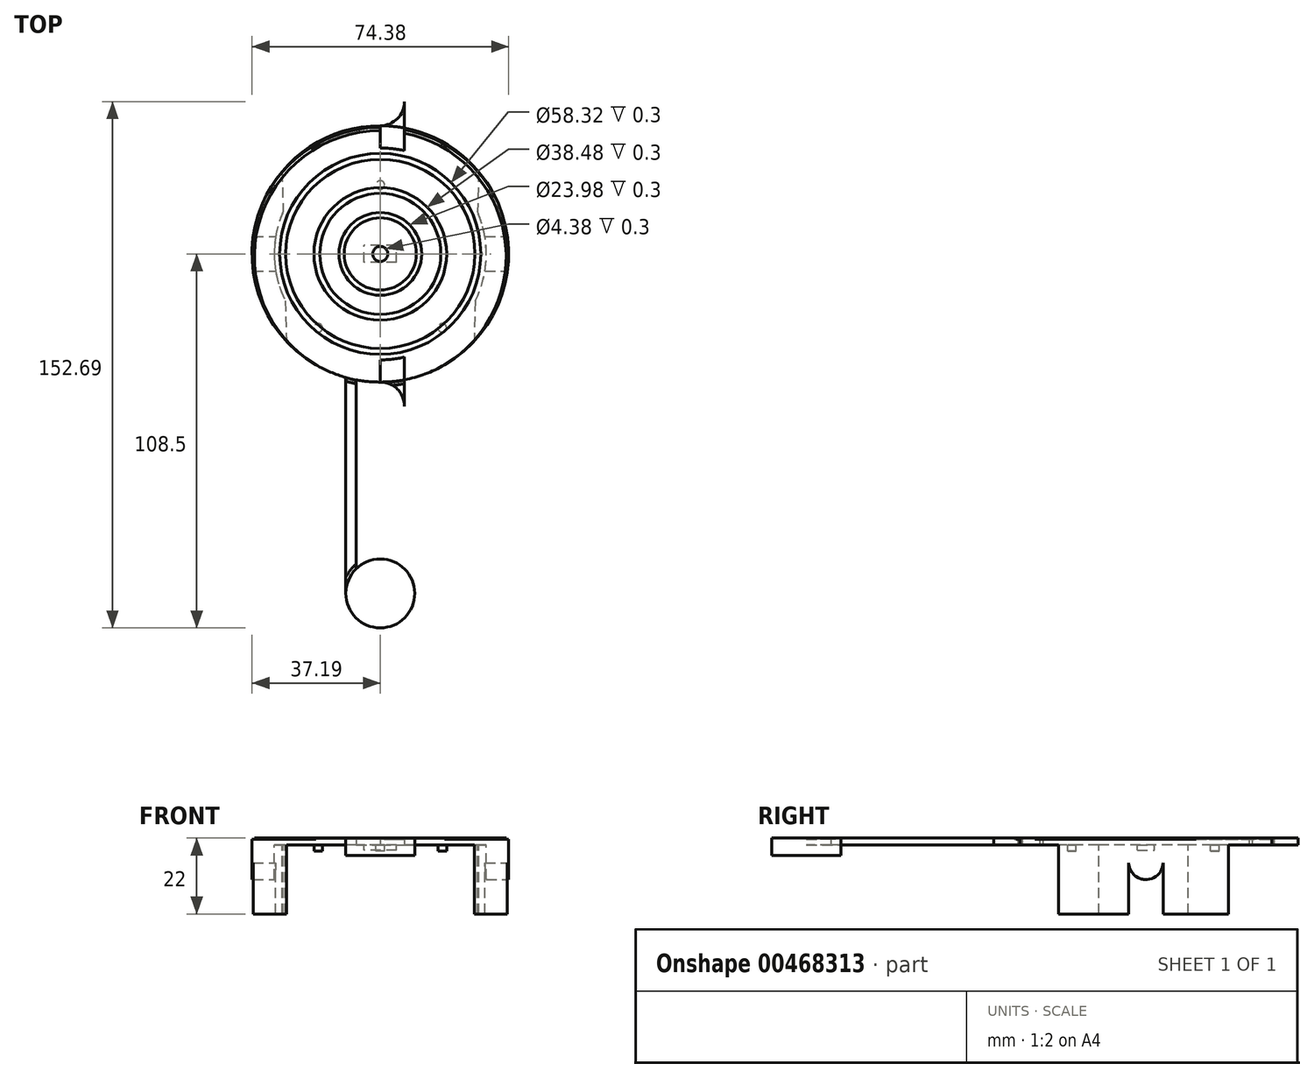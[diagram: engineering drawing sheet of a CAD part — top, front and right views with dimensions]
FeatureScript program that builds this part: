
annotation { "Feature Type Name" : "Feature", "Feature Type Description" : "" }
export const myFeature = defineFeature(function(context is Context, id is Id, definition is map)
    precondition{}
    {
        {
            var Q0;
            Q0=qCreatedBy(makeId("Top.planeOp"),FACE);
            var sketch = newSketch(context, id + "F0", { "sketchPlane" : qUnion([Q0])});
            skLineSegment(sketch, "E0.bottom", {"start": v(4.75, -2.5) * mm, "end": v(-4.75, -2.5) * mm});
            skLineSegment(sketch, "E0.top", {"start": v(4.75, 2.5) * mm, "end": v(-4.75, 2.5) * mm});
            skLineSegment(sketch, "E0.left", {"start": v(4.75, -2.5) * mm, "end": v(4.75, 2.5) * mm});
            skLineSegment(sketch, "E0.right", {"start": v(-4.75, -2.5) * mm, "end": v(-4.75, 2.5) * mm});
            skPoint(sketch, "E0.middle", {"position": v(0, 0) * mm});
            skLineSegment(sketch, "E1.bottom", {"start": v(5.25, 3) * mm, "end": v(-5.25, 3) * mm});
            skLineSegment(sketch, "E1.top", {"start": v(5.25, -3) * mm, "end": v(-5.25, -3) * mm});
            skLineSegment(sketch, "E1.left", {"start": v(5.25, 3) * mm, "end": v(5.25, -3) * mm});
            skLineSegment(sketch, "E1.right", {"start": v(-5.25, 3) * mm, "end": v(-5.25, -3) * mm});
            skCircle(sketch, "E2", {"center": v(0, 0) * mm, "radius": 37.2 * mm});
            skLineSegment(sketch, "E3", {"start": v(0, 0) * mm, "end": v(18, -21.45) * mm, "construction": true});
            skLineSegment(sketch, "E4", {"start": v(18, -21.45) * mm, "end": v(-18, -21.45) * mm});
            skLineSegment(sketch, "E5", {"start": v(-18, -21.45) * mm, "end": v(0, 0) * mm, "construction": true});
            skLineSegment(sketch, "E6", {"start": v(0, 0) * mm, "end": v(0, 20) * mm, "construction": true});
            skPoint(sketch, "E6.endSnap0", {"position": v(0, 3) * mm});
            skCircle(sketch, "E7", {"center": v(0, 20) * mm, "radius": 1.25 * mm});
            skCircle(sketch, "E8", {"center": v(18, -21.45) * mm, "radius": 1.25 * mm});
            skCircle(sketch, "E9", {"center": v(-18, -21.45) * mm, "radius": 1.25 * mm});
            skLineSegment(sketch, "E10", {"start": v(28.5, 23.9) * mm, "end": v(-28.5, 23.9) * mm, "construction": true});
            skLineSegment(sketch, "E11", {"start": v(27.25, -25.31) * mm, "end": v(-27.25, -25.31) * mm, "construction": true});
            skLineSegment(sketch, "E12", {"start": v(28.5, 23.9) * mm, "end": v(27.25, -25.31) * mm});
            skLineSegment(sketch, "E13", {"start": v(-28.5, 23.9) * mm, "end": v(-27.25, -25.31) * mm});
            skLineSegment(sketch, "E14", {"start": v(0, 0) * mm, "end": v(0, 108) * mm, "construction": true});
            skLineSegment(sketch, "E15", {"start": v(0, 0) * mm, "end": v(0, -98.5) * mm, "construction": true});
            skLineSegment(sketch, "E16.bottom", {"start": v(0, 108) * mm, "end": v(0, 108) * mm});
            skLineSegment(sketch, "E16.top", {"start": v(0, -98.5) * mm, "end": v(0, -98.5) * mm});
            skLineSegment(sketch, "E16.left", {"start": v(0, 108) * mm, "end": v(0, -98.5) * mm});
            skLineSegment(sketch, "E16.right", {"start": v(0, 108) * mm, "end": v(0, -98.5) * mm});
            skLineSegment(sketch, "E17.bottom", {"start": v(10, -98.5) * mm, "end": v(-10, -98.5) * mm});
            skLineSegment(sketch, "E17.top", {"start": v(10, 108) * mm, "end": v(-10, 108) * mm});
            skLineSegment(sketch, "E17.left", {"start": v(10, -98.5) * mm, "end": v(10, 108) * mm});
            skLineSegment(sketch, "E17.right", {"start": v(-10, -98.5) * mm, "end": v(-10, 108) * mm});
            skPoint(sketch, "E17.middle", {"position": v(0, 4.75) * mm});
            skCircle(sketch, "E18", {"center": v(0, 108) * mm, "radius": 10 * mm});
            skCircle(sketch, "E19", {"center": v(0, -98.5) * mm, "radius": 10 * mm});
            skCircle(sketch, "E20.0", {"center": v(0, 108) * mm, "radius": 7 * mm});
            skCircle(sketch, "E21", {"center": v(0, -98.5) * mm, "radius": 7 * mm});
            skLineSegment(sketch, "E22", {"start": v(7, 108) * mm, "end": v(7, -98.5) * mm});
            skLineSegment(sketch, "E23", {"start": v(-7, 108) * mm, "end": v(-7, -98.5) * mm});
            skLineSegment(sketch, "E24", {"start": v(-10, 37.2) * mm, "end": v(7, 37.2) * mm, "construction": true});
            skPoint(sketch, "E25", {"position": v(0, 37.2) * mm});
            skCircle(sketch, "E26", {"center": v(0, 44.2) * mm, "radius": 7 * mm});
            skPoint(sketch, "E27", {"position": v(0, -37.2) * mm});
            skCircle(sketch, "E28", {"center": v(0, -44.2) * mm, "radius": 7 * mm});
            skCircle(sketch, "E29", {"center": v(0, 108) * mm, "radius": 6.5 * mm});
            skCircle(sketch, "E30", {"center": v(0, 0) * mm, "radius": 30.75 * mm});
            skSolve(sketch);
        }
        {
            var Q0;
            {var subQ0=sQuery(id+"F0.wireOp",EDGE,"E12");Q0=makeQuery(id+"F0.imprint","IMPRINT",FACE,{"disambiguationData":[TD([[makeQuery(id+"F0.imprint","IMPRINT",EDGE,{"derivedFrom":subQ0}),1.0]])]});}
            var Q1;
            {var subQ0=sQuery(id+"F0.wireOp",EDGE,"E13");Q1=makeQuery(id+"F0.imprint","IMPRINT",FACE,{"disambiguationData":[TD([[makeQuery(id+"F0.imprint","IMPRINT",EDGE,{"derivedFrom":subQ0}),-1.0]])]});}
            extrude(context, id + "F1", {"entities" : qUnion([Q0, Q1]), "depth" : -20 * mm});
        }
        {
            var Q0;
            Q0=qCreatedBy(makeId("Right.planeOp"),FACE);
            var sketch = newSketch(context, id + "F2", { "sketchPlane" : qUnion([Q0])});
            skLineSegment(sketch, "E31.0.0", {"start": v(-13.66, 0) * mm, "end": v(12.25, 0) * mm});
            skLineSegment(sketch, "E31.0.1", {"start": v(12.25, 0) * mm, "end": v(12.25, -20) * mm});
            skLineSegment(sketch, "E31.0.2", {"start": v(12.25, -20) * mm, "end": v(-13.66, -20) * mm});
            skLineSegment(sketch, "E31.0.3", {"start": v(-13.66, -20) * mm, "end": v(-13.66, 0) * mm});
            skLineSegment(sketch, "E32.bottom", {"start": v(-5, 0) * mm, "end": v(5, 0) * mm});
            skLineSegment(sketch, "E32.top", {"start": v(-5, -20) * mm, "end": v(5, -20) * mm});
            skLineSegment(sketch, "E32.left", {"start": v(-5, 0) * mm, "end": v(-5, -20) * mm});
            skLineSegment(sketch, "E32.right", {"start": v(5, 0) * mm, "end": v(5, -20) * mm});
            skPoint(sketch, "E32.middle", {"position": v(0, -10) * mm});
            skCircle(sketch, "E33", {"center": v(0, -5) * mm, "radius": 5 * mm});
            skPoint(sketch, "E33.first.point", {"position": v(5, -5.19) * mm});
            skPoint(sketch, "E33.second.point", {"position": v(0, 0) * mm});
            skPoint(sketch, "E33.third.point", {"position": v(-5, -4.77) * mm});
            skSolve(sketch);
        }
        {
            var Q0;
            {var subQ0=sQuery(id+"F2.wireOp",EDGE,"E32.top");Q0=makeQuery(id+"F2.imprint","IMPRINT",FACE,{"disambiguationData":[TD([[makeQuery(id+"F2.imprint","IMPRINT",EDGE,{"derivedFrom":subQ0}),1.0]])]});}
            var Q1;
            {var subQ0=sQuery(id+"F2.wireOp",EDGE,"E33");var subQ2=sQuery(id+"F2.wireOp",EDGE,"E32.left");var subQ3=makeQuery(id+"F2.imprint","INTERSECT",VERTEX,{"disambiguationData":[OD(0.0)],"derivedFrom":[subQ2,subQ0]});Q1=makeQuery(id+"F2.imprint","IMPRINT",FACE,{"disambiguationData":[TD([[makeQuery(id+"F2.imprint","IMPRINT",EDGE,{"disambiguationData":[TD([[subQ3,-1.0]])],"derivedFrom":subQ2}),1.0]])]});}
            extrude(context, id + "F3", {"entities" : qUnion([Q0, Q1]), "operationType" : NewBodyOperationType.REMOVE, "endBound" : BoundingType.THROUGH_ALL, "oppositeDirection" : true, "depth" : 25 * mm, "hasSecondDirection" : true, "secondDirectionBound" : SecondDirectionBoundingType.THROUGH_ALL, "secondDirectionOppositeDirection" : false, "secondDirectionDepth" : 25 * mm});
        }
        {
            var Q0;
            Q0=makeQuery(id+"F0.imprint","IMPRINT",FACE,{"disambiguationData":[TD([[makeQuery(id+"F0.imprint","IMPRINT",EDGE,{"derivedFrom":sQuery(id+"F0.wireOp",EDGE,"E9")}),1.0]])]});
            var Q1;
            Q1=makeQuery(id+"F0.imprint","IMPRINT",FACE,{"disambiguationData":[TD([[makeQuery(id+"F0.imprint","IMPRINT",EDGE,{"derivedFrom":sQuery(id+"F0.wireOp",EDGE,"E8")}),1.0]])]});
            var Q2;
            Q2=makeQuery(id+"F0.imprint","IMPRINT",FACE,{"disambiguationData":[TD([[makeQuery(id+"F0.imprint","IMPRINT",EDGE,{"derivedFrom":sQuery(id+"F0.wireOp",EDGE,"E7")}),1.0]])]});
            extrude(context, id + "F4", {"entities" : qUnion([Q0, Q1, Q2]), "operationType" : NewBodyOperationType.ADD, "depth" : -1.75 * mm});
        }
        {
            var Q0;
            Q0=makeQuery(id+"F0.imprint","IMPRINT",FACE,{"disambiguationData":[TD([[makeQuery(id+"F0.imprint","IMPRINT",EDGE,{"derivedFrom":sQuery(id+"F0.wireOp",EDGE,"E0.bottom")}),-1.0]])]});
            var Q1;
            Q1=makeQuery(id+"F0.imprint","IMPRINT",FACE,{"disambiguationData":[TD([[makeQuery(id+"F0.imprint","IMPRINT",EDGE,{"derivedFrom":sQuery(id+"F0.wireOp",EDGE,"E1.bottom")}),-1.0]])]});
            var Q2;
            Q2=makeQuery(id+"F0.imprint","IMPRINT",FACE,{"disambiguationData":[TD([[makeQuery(id+"F0.imprint","IMPRINT",EDGE,{"derivedFrom":sQuery(id+"F0.wireOp",EDGE,"E0.bottom")}),1.0]])]});
            var Q3;
            Q3=makeQuery(id+"F4.opExtrude","CAP_FACE",FACE,{"disambiguationData":[OSD([sQuery(id+"F0.wireOp",EDGE,"E7")])],"isStart":true});
            var Q4;
            Q4=makeQuery(id+"F4.opExtrude","CAP_FACE",FACE,{"disambiguationData":[OSD([sQuery(id+"F0.wireOp",EDGE,"E9")])],"isStart":true});
            var Q5;
            Q5=makeQuery(id+"F4.opExtrude","CAP_FACE",FACE,{"disambiguationData":[OSD([sQuery(id+"F0.wireOp",EDGE,"E8")])],"isStart":true});
            var Q6;
            Q6=makeQuery(id+"F0.imprint","IMPRINT",FACE,{"disambiguationData":[TD([[makeQuery(id+"F0.imprint","IMPRINT",EDGE,{"derivedFrom":sQuery(id+"F0.wireOp",EDGE,"E7")}),1.0]])]});
            var Q7;
            Q7=makeQuery(id+"F0.imprint","IMPRINT",FACE,{"disambiguationData":[TD([[makeQuery(id+"F0.imprint","IMPRINT",EDGE,{"derivedFrom":sQuery(id+"F0.wireOp",EDGE,"E8")}),1.0]])]});
            var Q8;
            Q8=makeQuery(id+"F4.opExtrude","CAP_FACE",FACE,{"disambiguationData":[OSD([sQuery(id+"F0.wireOp",EDGE,"E7")])],"isStart":false});
            var Q9;
            Q9=makeQuery(id+"F4.opExtrude","CAP_FACE",FACE,{"disambiguationData":[OSD([sQuery(id+"F0.wireOp",EDGE,"E9")])],"isStart":false});
            var Q10;
            Q10=makeQuery(id+"F4.opExtrude","CAP_FACE",FACE,{"disambiguationData":[OSD([sQuery(id+"F0.wireOp",EDGE,"E8")])],"isStart":false});
            var Q11;
            {var subQ0=sQuery(id+"F0.wireOp",EDGE,"E12");Q11=makeQuery(id+"F0.imprint","IMPRINT",FACE,{"disambiguationData":[TD([[makeQuery(id+"F0.imprint","IMPRINT",EDGE,{"derivedFrom":subQ0}),1.0]])]});}
            var Q12;
            {var subQ0=sQuery(id+"F0.wireOp",EDGE,"E13");Q12=makeQuery(id+"F0.imprint","IMPRINT",FACE,{"disambiguationData":[TD([[makeQuery(id+"F0.imprint","IMPRINT",EDGE,{"derivedFrom":subQ0}),-1.0]])]});}
            var Q13;
            Q13=makeQuery(id+"F0.imprint","IMPRINT",FACE,{"disambiguationData":[TD([[makeQuery(id+"F0.imprint","IMPRINT",EDGE,{"derivedFrom":sQuery(id+"F0.wireOp",EDGE,"E9")}),-1.0]])]});
            var Q14;
            Q14=makeQuery(id+"F0.imprint","IMPRINT",FACE,{"disambiguationData":[TD([[makeQuery(id+"F0.imprint","IMPRINT",EDGE,{"derivedFrom":sQuery(id+"F0.wireOp",EDGE,"E8")}),-1.0]])]});
            var Q15;
            {var subQ0=sQuery(id+"F0.wireOp",EDGE,"E17.left");var subQ1=sQuery(id+"F0.wireOp",EDGE,"E2");var subQ2=makeQuery(id+"F0.imprint","INTERSECT",VERTEX,{"disambiguationData":[OD(1.0)],"derivedFrom":[subQ1,subQ0]});Q15=makeQuery(id+"F0.imprint","IMPRINT",FACE,{"disambiguationData":[TD([[makeQuery(id+"F0.imprint","IMPRINT",EDGE,{"disambiguationData":[TD([[subQ2,1.0]])],"derivedFrom":subQ1}),1.0]])]});}
            var Q16;
            {var subQ0=sQuery(id+"F0.wireOp",EDGE,"E17.right");var subQ1=sQuery(id+"F0.wireOp",EDGE,"E2");var subQ2=makeQuery(id+"F0.imprint","INTERSECT",VERTEX,{"disambiguationData":[OD(1.0)],"derivedFrom":[subQ1,subQ0]});Q16=makeQuery(id+"F0.imprint","IMPRINT",FACE,{"disambiguationData":[TD([[makeQuery(id+"F0.imprint","IMPRINT",EDGE,{"disambiguationData":[TD([[subQ2,-1.0]])],"derivedFrom":subQ1}),1.0]])]});}
            var Q17;
            {var subQ0=sQuery(id+"F0.wireOp",EDGE,"E23");var subQ1=sQuery(id+"F0.wireOp",EDGE,"E2");var subQ2=makeQuery(id+"F0.imprint","INTERSECT",VERTEX,{"disambiguationData":[OD(1.0)],"derivedFrom":[subQ1,subQ0]});Q17=makeQuery(id+"F0.imprint","IMPRINT",FACE,{"disambiguationData":[TD([[makeQuery(id+"F0.imprint","IMPRINT",EDGE,{"disambiguationData":[TD([[subQ2,-1.0]])],"derivedFrom":subQ1}),1.0]])]});}
            var Q18;
            {var subQ1=sQuery(id+"F0.wireOp",EDGE,"E2");var subQ7=sQuery(id+"F0.wireOp",EDGE,"JaR2KPRH-AKVw-h21Q-BMjd-ttM7igPpjMCP");var subQ9=makeQuery(id+"F0.imprint","INTERSECT",VERTEX,{"disambiguationData":[OD(1.0)],"derivedFrom":[subQ1,subQ7]});Q18=makeQuery(id+"F0.imprint","IMPRINT",FACE,{"disambiguationData":[TD([[makeQuery(id+"F0.imprint","IMPRINT",EDGE,{"disambiguationData":[TD([[subQ9,-1.0]])],"derivedFrom":subQ1}),1.0]])]});}
            var Q19;
            {var subQ0=sQuery(id+"F0.wireOp",EDGE,"E17.right");var subQ1=sQuery(id+"F0.wireOp",EDGE,"E2");var subQ2=makeQuery(id+"F0.imprint","INTERSECT",VERTEX,{"disambiguationData":[OD(0.0)],"derivedFrom":[subQ1,subQ0]});Q19=makeQuery(id+"F0.imprint","IMPRINT",FACE,{"disambiguationData":[TD([[makeQuery(id+"F0.imprint","IMPRINT",EDGE,{"disambiguationData":[TD([[subQ2,1.0]])],"derivedFrom":subQ1}),1.0]])]});}
            var Q20;
            {var subQ0=sQuery(id+"F0.wireOp",EDGE,"E17.left");var subQ1=sQuery(id+"F0.wireOp",EDGE,"E2");var subQ2=makeQuery(id+"F0.imprint","INTERSECT",VERTEX,{"disambiguationData":[OD(0.0)],"derivedFrom":[subQ1,subQ0]});Q20=makeQuery(id+"F0.imprint","IMPRINT",FACE,{"disambiguationData":[TD([[makeQuery(id+"F0.imprint","IMPRINT",EDGE,{"disambiguationData":[TD([[subQ2,-1.0]])],"derivedFrom":subQ1}),1.0]])]});}
            var Q21;
            {var subQ0=sQuery(id+"F0.wireOp",EDGE,"E22");var subQ5=sQuery(id+"F0.wireOp",EDGE,"E4");var subQ6=makeQuery(id+"F0.imprint","INTERSECT",VERTEX,{"derivedFrom":[subQ5,subQ0]});Q21=makeQuery(id+"F0.imprint","IMPRINT",FACE,{"disambiguationData":[TD([[makeQuery(id+"F0.imprint","IMPRINT",EDGE,{"disambiguationData":[TD([[subQ6,-1.0]])],"derivedFrom":subQ5}),1.0]])]});}
            var Q22;
            {var subQ11=sQuery(id+"F0.wireOp",EDGE,"E1.left");Q22=makeQuery(id+"F0.imprint","IMPRINT",FACE,{"disambiguationData":[TD([[makeQuery(id+"F0.imprint","IMPRINT",EDGE,{"derivedFrom":subQ11}),1.0]])]});}
            var Q23;
            {var subQ0=sQuery(id+"F0.wireOp",EDGE,"E13");var subQ1=sQuery(id+"F0.wireOp",EDGE,"E2");var subQ2=makeQuery(id+"F0.imprint","INTERSECT",VERTEX,{"disambiguationData":[OD(0.0)],"derivedFrom":[subQ1,subQ0]});Q23=makeQuery(id+"F0.imprint","IMPRINT",FACE,{"disambiguationData":[TD([[makeQuery(id+"F0.imprint","IMPRINT",EDGE,{"disambiguationData":[TD([[subQ2,1.0]])],"derivedFrom":subQ1}),1.0]])]});}
            var Q24;
            {var subQ0=sQuery(id+"F0.wireOp",EDGE,"E23");var subQ1=sQuery(id+"F0.wireOp",EDGE,"E2");var subQ2=makeQuery(id+"F0.imprint","INTERSECT",VERTEX,{"disambiguationData":[OD(0.0)],"derivedFrom":[subQ1,subQ0]});Q24=makeQuery(id+"F0.imprint","IMPRINT",FACE,{"disambiguationData":[TD([[makeQuery(id+"F0.imprint","IMPRINT",EDGE,{"disambiguationData":[TD([[subQ2,-1.0]])],"derivedFrom":subQ0}),1.0]])]});}
            var Q25;
            {var subQ0=sQuery(id+"F0.wireOp",EDGE,"E22");var subQ1=sQuery(id+"F0.wireOp",EDGE,"E2");var subQ2=makeQuery(id+"F0.imprint","INTERSECT",VERTEX,{"disambiguationData":[OD(0.0)],"derivedFrom":[subQ1,subQ0]});Q25=makeQuery(id+"F0.imprint","IMPRINT",FACE,{"disambiguationData":[TD([[makeQuery(id+"F0.imprint","IMPRINT",EDGE,{"disambiguationData":[TD([[subQ2,-1.0]])],"derivedFrom":subQ0}),-1.0]])]});}
            var Q26;
            {var subQ0=sQuery(id+"F0.wireOp",EDGE,"E12");var subQ1=sQuery(id+"F0.wireOp",EDGE,"E2");var subQ2=makeQuery(id+"F0.imprint","INTERSECT",VERTEX,{"disambiguationData":[OD(0.0)],"derivedFrom":[subQ1,subQ0]});Q26=makeQuery(id+"F0.imprint","IMPRINT",FACE,{"disambiguationData":[TD([[makeQuery(id+"F0.imprint","IMPRINT",EDGE,{"disambiguationData":[TD([[subQ2,-1.0]])],"derivedFrom":subQ1}),1.0]])]});}
            var Q27;
            {var subQ0=sQuery(id+"F0.wireOp",EDGE,"E17.left");var subQ1=sQuery(id+"F0.wireOp",EDGE,"E4");var subQ2=makeQuery(id+"F0.imprint","INTERSECT",VERTEX,{"derivedFrom":[subQ1,subQ0]});Q27=makeQuery(id+"F0.imprint","IMPRINT",FACE,{"disambiguationData":[TD([[makeQuery(id+"F0.imprint","IMPRINT",EDGE,{"disambiguationData":[TD([[subQ2,-1.0]])],"derivedFrom":subQ1}),-1.0]])]});}
            var Q28;
            {var subQ0=sQuery(id+"F0.wireOp",EDGE,"E17.right");var subQ1=sQuery(id+"F0.wireOp",EDGE,"E4");var subQ2=makeQuery(id+"F0.imprint","INTERSECT",VERTEX,{"derivedFrom":[subQ1,subQ0]});Q28=makeQuery(id+"F0.imprint","IMPRINT",FACE,{"disambiguationData":[TD([[makeQuery(id+"F0.imprint","IMPRINT",EDGE,{"disambiguationData":[TD([[subQ2,1.0]])],"derivedFrom":subQ1}),-1.0]])]});}
            var Q29;
            {var subQ0=sQuery(id+"F0.wireOp",EDGE,"E30");var subQ1=sQuery(id+"F0.wireOp",EDGE,"E12");var subQ2=makeQuery(id+"F0.imprint","INTERSECT",VERTEX,{"disambiguationData":[OD(0.0)],"derivedFrom":[subQ1,subQ0]});Q29=makeQuery(id+"F0.imprint","IMPRINT",FACE,{"disambiguationData":[TD([[makeQuery(id+"F0.imprint","IMPRINT",EDGE,{"disambiguationData":[TD([[subQ2,-1.0]])],"derivedFrom":subQ1}),1.0]])]});}
            var Q30;
            {var subQ0=sQuery(id+"F0.wireOp",EDGE,"E12");var subQ1=sQuery(id+"F0.wireOp",EDGE,"E2");var subQ2=makeQuery(id+"F0.imprint","INTERSECT",VERTEX,{"disambiguationData":[OD(1.0)],"derivedFrom":[subQ1,subQ0]});Q30=makeQuery(id+"F0.imprint","IMPRINT",FACE,{"disambiguationData":[TD([[makeQuery(id+"F0.imprint","IMPRINT",EDGE,{"disambiguationData":[TD([[subQ2,1.0]])],"derivedFrom":subQ1}),1.0]])]});}
            var Q31;
            {var subQ0=sQuery(id+"F0.wireOp",EDGE,"E22");var subQ1=sQuery(id+"F0.wireOp",EDGE,"E2");var subQ2=makeQuery(id+"F0.imprint","INTERSECT",VERTEX,{"disambiguationData":[OD(1.0)],"derivedFrom":[subQ1,subQ0]});Q31=makeQuery(id+"F0.imprint","IMPRINT",FACE,{"disambiguationData":[TD([[makeQuery(id+"F0.imprint","IMPRINT",EDGE,{"disambiguationData":[TD([[subQ2,1.0]])],"derivedFrom":subQ0}),-1.0]])]});}
            var Q32;
            {var subQ0=sQuery(id+"F0.wireOp",EDGE,"E17.left");var subQ1=sQuery(id+"F0.wireOp",EDGE,"E4");var subQ2=makeQuery(id+"F0.imprint","INTERSECT",VERTEX,{"derivedFrom":[subQ1,subQ0]});Q32=makeQuery(id+"F0.imprint","IMPRINT",FACE,{"disambiguationData":[TD([[makeQuery(id+"F0.imprint","IMPRINT",EDGE,{"disambiguationData":[TD([[subQ2,-1.0]])],"derivedFrom":subQ1}),1.0]])]});}
            var Q33;
            {var subQ0=sQuery(id+"F0.wireOp",EDGE,"E16.left");var subQ1=sQuery(id+"F0.wireOp",EDGE,"E4");var subQ2=makeQuery(id+"F0.imprint","INTERSECT",VERTEX,{"derivedFrom":[subQ1,subQ0]});Q33=makeQuery(id+"F0.imprint","IMPRINT",FACE,{"disambiguationData":[TD([[makeQuery(id+"F0.imprint","IMPRINT",EDGE,{"disambiguationData":[TD([[subQ2,-1.0]])],"derivedFrom":subQ1}),1.0]])]});}
            var Q34;
            {var subQ0=sQuery(id+"F0.wireOp",EDGE,"E17.right");var subQ1=sQuery(id+"F0.wireOp",EDGE,"E4");var subQ2=makeQuery(id+"F0.imprint","INTERSECT",VERTEX,{"derivedFrom":[subQ1,subQ0]});Q34=makeQuery(id+"F0.imprint","IMPRINT",FACE,{"disambiguationData":[TD([[makeQuery(id+"F0.imprint","IMPRINT",EDGE,{"disambiguationData":[TD([[subQ2,1.0]])],"derivedFrom":subQ1}),1.0]])]});}
            var Q35;
            {var subQ0=sQuery(id+"F0.wireOp",EDGE,"E13");var subQ1=sQuery(id+"F0.wireOp",EDGE,"E2");var subQ2=makeQuery(id+"F0.imprint","INTERSECT",VERTEX,{"disambiguationData":[OD(1.0)],"derivedFrom":[subQ1,subQ0]});Q35=makeQuery(id+"F0.imprint","IMPRINT",FACE,{"disambiguationData":[TD([[makeQuery(id+"F0.imprint","IMPRINT",EDGE,{"disambiguationData":[TD([[subQ2,-1.0]])],"derivedFrom":subQ1}),1.0]])]});}
            var Q36;
            {var subQ0=sQuery(id+"F0.wireOp",EDGE,"E30");var subQ1=sQuery(id+"F0.wireOp",EDGE,"E13");var subQ2=makeQuery(id+"F0.imprint","INTERSECT",VERTEX,{"disambiguationData":[OD(0.0)],"derivedFrom":[subQ1,subQ0]});Q36=makeQuery(id+"F0.imprint","IMPRINT",FACE,{"disambiguationData":[TD([[makeQuery(id+"F0.imprint","IMPRINT",EDGE,{"disambiguationData":[TD([[subQ2,-1.0]])],"derivedFrom":subQ1}),-1.0]])]});}
            var Q37;
            {var subQ0=sQuery(id+"F0.wireOp",EDGE,"E23");var subQ6=sQuery(id+"F0.wireOp",EDGE,"nyIkWiiJ-WDHy-3Xyo-in1a-z6gPwWDwMGwc");var subQ7=makeQuery(id+"F0.imprint","INTERSECT",VERTEX,{"disambiguationData":[OD(1.0)],"derivedFrom":[subQ0,subQ6]});Q37=makeQuery(id+"F0.imprint","IMPRINT",FACE,{"disambiguationData":[TD([[makeQuery(id+"F0.imprint","IMPRINT",EDGE,{"disambiguationData":[TD([[subQ7,-1.0]])],"derivedFrom":subQ0}),-1.0]])]});}
            var Q38;
            {var subQ0=sQuery(id+"F0.wireOp",EDGE,"E22");var subQ4=sQuery(id+"F0.wireOp",EDGE,"nyIkWiiJ-WDHy-3Xyo-in1a-z6gPwWDwMGwc");var subQ5=makeQuery(id+"F0.imprint","INTERSECT",VERTEX,{"disambiguationData":[OD(1.0)],"derivedFrom":[subQ0,subQ4]});Q38=makeQuery(id+"F0.imprint","IMPRINT",FACE,{"disambiguationData":[TD([[makeQuery(id+"F0.imprint","IMPRINT",EDGE,{"disambiguationData":[TD([[subQ5,-1.0]])],"derivedFrom":subQ0}),1.0]])]});}
            var Q39;
            {var subQ0=sQuery(id+"F0.wireOp",EDGE,"E19");var subQ1=sQuery(id+"F0.wireOp",EDGE,"E17.bottom");var subQ2=makeQuery(id+"F0.imprint","INTERSECT",VERTEX,{"derivedFrom":[subQ1,sQuery(id+"F0.wireOp",EDGE,"E17.left"),subQ0]});Q39=makeQuery(id+"F0.imprint","IMPRINT",FACE,{"disambiguationData":[TD([[makeQuery(id+"F0.imprint","IMPRINT",EDGE,{"disambiguationData":[TD([[subQ2,-1.0]])],"derivedFrom":subQ1}),1.0]])]});}
            var Q40;
            {var subQ0=sQuery(id+"F0.wireOp",EDGE,"E17.bottom");var subQ1=makeQuery(id+"F0.imprint","INTERSECT",VERTEX,{"derivedFrom":[sQuery(id+"F0.wireOp",EDGE,"E16.left"),subQ0]});Q40=makeQuery(id+"F0.imprint","IMPRINT",FACE,{"disambiguationData":[TD([[makeQuery(id+"F0.imprint","IMPRINT",EDGE,{"disambiguationData":[TD([[subQ1,1.0]])],"derivedFrom":subQ0}),1.0]])]});}
            var Q41;
            {var subQ0=sQuery(id+"F0.wireOp",EDGE,"E17.bottom");var subQ1=sQuery(id+"F0.wireOp",EDGE,"E16.left");var subQ2=makeQuery(id+"F0.imprint","INTERSECT",VERTEX,{"derivedFrom":[subQ1,subQ0]});Q41=makeQuery(id+"F0.imprint","IMPRINT",FACE,{"disambiguationData":[TD([[makeQuery(id+"F0.imprint","IMPRINT",EDGE,{"disambiguationData":[TD([[subQ2,1.0]])],"derivedFrom":subQ1}),1.0]])]});}
            var Q42;
            {var subQ0=sQuery(id+"F0.wireOp",EDGE,"E17.bottom");var subQ1=sQuery(id+"F0.wireOp",EDGE,"E16.left");var subQ2=makeQuery(id+"F0.imprint","INTERSECT",VERTEX,{"derivedFrom":[subQ1,subQ0]});Q42=makeQuery(id+"F0.imprint","IMPRINT",FACE,{"disambiguationData":[TD([[makeQuery(id+"F0.imprint","IMPRINT",EDGE,{"disambiguationData":[TD([[subQ2,1.0]])],"derivedFrom":subQ1}),-1.0]])]});}
            var Q43;
            {var subQ0=sQuery(id+"F0.wireOp",EDGE,"E19");var subQ1=sQuery(id+"F0.wireOp",EDGE,"E16.left");var subQ2=makeQuery(id+"F0.imprint","INTERSECT",VERTEX,{"derivedFrom":[subQ1,subQ0]});Q43=makeQuery(id+"F0.imprint","IMPRINT",FACE,{"disambiguationData":[TD([[makeQuery(id+"F0.imprint","IMPRINT",EDGE,{"disambiguationData":[TD([[subQ2,-1.0]])],"derivedFrom":subQ1}),-1.0]])]});}
            var Q44;
            {var subQ0=sQuery(id+"F0.wireOp",EDGE,"E19");var subQ1=sQuery(id+"F0.wireOp",EDGE,"E16.left");var subQ2=makeQuery(id+"F0.imprint","INTERSECT",VERTEX,{"derivedFrom":[subQ1,subQ0]});Q44=makeQuery(id+"F0.imprint","IMPRINT",FACE,{"disambiguationData":[TD([[makeQuery(id+"F0.imprint","IMPRINT",EDGE,{"disambiguationData":[TD([[subQ2,-1.0]])],"derivedFrom":subQ1}),1.0]])]});}
            var Q45;
            {var subQ0=sQuery(id+"F0.wireOp",EDGE,"E19");var subQ3=sQuery(id+"F0.wireOp",EDGE,"E22");var subQ5=makeQuery(id+"F0.imprint","INTERSECT",VERTEX,{"derivedFrom":[subQ0,subQ3]});Q45=makeQuery(id+"F0.imprint","IMPRINT",FACE,{"disambiguationData":[TD([[makeQuery(id+"F0.imprint","IMPRINT",EDGE,{"disambiguationData":[TD([[subQ5,1.0]])],"derivedFrom":subQ0}),1.0]])]});}
            var Q46;
            {var subQ0=sQuery(id+"F0.wireOp",EDGE,"E19");var subQ3=sQuery(id+"F0.wireOp",EDGE,"E23");var subQ5=makeQuery(id+"F0.imprint","INTERSECT",VERTEX,{"derivedFrom":[subQ0,subQ3]});Q46=makeQuery(id+"F0.imprint","IMPRINT",FACE,{"disambiguationData":[TD([[makeQuery(id+"F0.imprint","IMPRINT",EDGE,{"disambiguationData":[TD([[subQ5,-1.0]])],"derivedFrom":subQ0}),1.0]])]});}
            var Q47;
            {var subQ0=sQuery(id+"F0.wireOp",EDGE,"nyIkWiiJ-WDHy-3Xyo-in1a-z6gPwWDwMGwc");var subQ1=sQuery(id+"F0.wireOp",EDGE,"E23");var subQ2=makeQuery(id+"F0.imprint","INTERSECT",VERTEX,{"disambiguationData":[OD(1.0)],"derivedFrom":[subQ1,subQ0]});Q47=makeQuery(id+"F0.imprint","IMPRINT",FACE,{"disambiguationData":[TD([[makeQuery(id+"F0.imprint","IMPRINT",EDGE,{"disambiguationData":[TD([[subQ2,-1.0]])],"derivedFrom":subQ1}),1.0]])]});}
            var Q48;
            {var subQ0=sQuery(id+"F0.wireOp",EDGE,"nyIkWiiJ-WDHy-3Xyo-in1a-z6gPwWDwMGwc");var subQ1=sQuery(id+"F0.wireOp",EDGE,"E22");var subQ2=makeQuery(id+"F0.imprint","INTERSECT",VERTEX,{"disambiguationData":[OD(1.0)],"derivedFrom":[subQ1,subQ0]});Q48=makeQuery(id+"F0.imprint","IMPRINT",FACE,{"disambiguationData":[TD([[makeQuery(id+"F0.imprint","IMPRINT",EDGE,{"disambiguationData":[TD([[subQ2,-1.0]])],"derivedFrom":subQ1}),-1.0]])]});}
            var Q49;
            {var subQ0=sQuery(id+"F0.wireOp",EDGE,"E17.right");var subQ1=sQuery(id+"F0.wireOp",EDGE,"E2");var subQ2=makeQuery(id+"F0.imprint","INTERSECT",VERTEX,{"disambiguationData":[OD(1.0)],"derivedFrom":[subQ1,subQ0]});Q49=makeQuery(id+"F0.imprint","IMPRINT",FACE,{"disambiguationData":[TD([[makeQuery(id+"F0.imprint","IMPRINT",EDGE,{"disambiguationData":[TD([[subQ2,-1.0]])],"derivedFrom":subQ1}),-1.0]])]});}
            var Q50;
            {var subQ0=sQuery(id+"F0.wireOp",EDGE,"E22");var subQ1=sQuery(id+"F0.wireOp",EDGE,"E2");var subQ2=makeQuery(id+"F0.imprint","INTERSECT",VERTEX,{"disambiguationData":[OD(1.0)],"derivedFrom":[subQ1,subQ0]});Q50=makeQuery(id+"F0.imprint","IMPRINT",FACE,{"disambiguationData":[TD([[makeQuery(id+"F0.imprint","IMPRINT",EDGE,{"disambiguationData":[TD([[subQ2,-1.0]])],"derivedFrom":subQ1}),-1.0]])]});}
            extrude(context, id + "F5", {"entities" : qUnion([Q0, Q1, Q2, Q3, Q4, Q5, Q6, Q7, Q8, Q9, Q10, Q11, Q12, Q13, Q14, Q15, Q16, Q17, Q18, Q19, Q20, Q21, Q22, Q23, Q24, Q25, Q26, Q27, Q28, Q29, Q30, Q31, Q32, Q33, Q34, Q35, Q36, Q37, Q38, Q39, Q40, Q41, Q42, Q43, Q44, Q45, Q46, Q47, Q48, Q49, Q50]), "operationType" : NewBodyOperationType.ADD, "depth" : 2 * mm});
        }
        {
            var Q0;
            Q0=makeQuery(id+"F0.imprint","IMPRINT",FACE,{"disambiguationData":[TD([[makeQuery(id+"F0.imprint","IMPRINT",EDGE,{"derivedFrom":sQuery(id+"F0.wireOp",EDGE,"E0.bottom")}),-1.0]])]});
            extrude(context, id + "F6", {"entities" : qUnion([Q0]), "operationType" : NewBodyOperationType.ADD, "depth" : -1.5 * mm});
        }
        {
            var Q0;
            {var subQ0=sQuery(id+"F0.wireOp",EDGE,"E19");var subQ1=sQuery(id+"F0.wireOp",EDGE,"E16.left");var subQ2=makeQuery(id+"F0.imprint","INTERSECT",VERTEX,{"derivedFrom":[subQ1,subQ0]});Q0=makeQuery(id+"F0.imprint","IMPRINT",FACE,{"disambiguationData":[TD([[makeQuery(id+"F0.imprint","IMPRINT",EDGE,{"disambiguationData":[TD([[subQ2,-1.0]])],"derivedFrom":subQ1}),-1.0]])]});}
            var Q1;
            {var subQ0=sQuery(id+"F0.wireOp",EDGE,"E19");var subQ3=sQuery(id+"F0.wireOp",EDGE,"E23");var subQ5=makeQuery(id+"F0.imprint","INTERSECT",VERTEX,{"derivedFrom":[subQ0,subQ3]});Q1=makeQuery(id+"F0.imprint","IMPRINT",FACE,{"disambiguationData":[TD([[makeQuery(id+"F0.imprint","IMPRINT",EDGE,{"disambiguationData":[TD([[subQ5,-1.0]])],"derivedFrom":subQ0}),1.0]])]});}
            var Q2;
            {var subQ0=sQuery(id+"F0.wireOp",EDGE,"E19");var subQ1=sQuery(id+"F0.wireOp",EDGE,"E17.bottom");var subQ2=makeQuery(id+"F0.imprint","INTERSECT",VERTEX,{"derivedFrom":[subQ1,sQuery(id+"F0.wireOp",EDGE,"E17.left"),subQ0]});Q2=makeQuery(id+"F0.imprint","IMPRINT",FACE,{"disambiguationData":[TD([[makeQuery(id+"F0.imprint","IMPRINT",EDGE,{"disambiguationData":[TD([[subQ2,-1.0]])],"derivedFrom":subQ1}),1.0]])]});}
            var Q3;
            {var subQ0=sQuery(id+"F0.wireOp",EDGE,"E17.bottom");var subQ1=makeQuery(id+"F0.imprint","INTERSECT",VERTEX,{"derivedFrom":[sQuery(id+"F0.wireOp",EDGE,"E16.left"),subQ0]});Q3=makeQuery(id+"F0.imprint","IMPRINT",FACE,{"disambiguationData":[TD([[makeQuery(id+"F0.imprint","IMPRINT",EDGE,{"disambiguationData":[TD([[subQ1,1.0]])],"derivedFrom":subQ0}),1.0]])]});}
            var Q4;
            {var subQ0=sQuery(id+"F0.wireOp",EDGE,"E17.bottom");var subQ1=sQuery(id+"F0.wireOp",EDGE,"E16.left");var subQ2=makeQuery(id+"F0.imprint","INTERSECT",VERTEX,{"derivedFrom":[subQ1,subQ0]});Q4=makeQuery(id+"F0.imprint","IMPRINT",FACE,{"disambiguationData":[TD([[makeQuery(id+"F0.imprint","IMPRINT",EDGE,{"disambiguationData":[TD([[subQ2,1.0]])],"derivedFrom":subQ1}),-1.0]])]});}
            var Q5;
            {var subQ0=sQuery(id+"F0.wireOp",EDGE,"E17.bottom");var subQ1=sQuery(id+"F0.wireOp",EDGE,"E16.left");var subQ2=makeQuery(id+"F0.imprint","INTERSECT",VERTEX,{"derivedFrom":[subQ1,subQ0]});Q5=makeQuery(id+"F0.imprint","IMPRINT",FACE,{"disambiguationData":[TD([[makeQuery(id+"F0.imprint","IMPRINT",EDGE,{"disambiguationData":[TD([[subQ2,1.0]])],"derivedFrom":subQ1}),1.0]])]});}
            var Q6;
            {var subQ0=sQuery(id+"F0.wireOp",EDGE,"E19");var subQ3=sQuery(id+"F0.wireOp",EDGE,"E22");var subQ5=makeQuery(id+"F0.imprint","INTERSECT",VERTEX,{"derivedFrom":[subQ0,subQ3]});Q6=makeQuery(id+"F0.imprint","IMPRINT",FACE,{"disambiguationData":[TD([[makeQuery(id+"F0.imprint","IMPRINT",EDGE,{"disambiguationData":[TD([[subQ5,1.0]])],"derivedFrom":subQ0}),1.0]])]});}
            var Q7;
            {var subQ0=sQuery(id+"F0.wireOp",EDGE,"E19");var subQ1=sQuery(id+"F0.wireOp",EDGE,"E16.left");var subQ2=makeQuery(id+"F0.imprint","INTERSECT",VERTEX,{"derivedFrom":[subQ1,subQ0]});Q7=makeQuery(id+"F0.imprint","IMPRINT",FACE,{"disambiguationData":[TD([[makeQuery(id+"F0.imprint","IMPRINT",EDGE,{"disambiguationData":[TD([[subQ2,-1.0]])],"derivedFrom":subQ1}),1.0]])]});}
            extrude(context, id + "F7", {"entities" : qUnion([Q0, Q1, Q2, Q3, Q4, Q5, Q6, Q7]), "operationType" : NewBodyOperationType.ADD, "depth" : -3 * mm});
        }
        {
            var Q0;
            Q0=makeQuery(id+"F5.opExtrude","CAP_FACE",FACE,{"disambiguationData":[OSD([sQuery(id+"F0.wireOp",EDGE,"E2"),sQuery(id+"F0.wireOp",EDGE,"E9"),sQuery(id+"F0.wireOp",EDGE,"E17.left"),sQuery(id+"F0.wireOp",EDGE,"E17.right"),sQuery(id+"F0.wireOp",EDGE,"E19"),sQuery(id+"F0.wireOp",EDGE,"E22"),sQuery(id+"F0.wireOp",EDGE,"E23"),sQuery(id+"F0.wireOp",EDGE,"E28")])],"isStart":false});
            var sketch = newSketch(context, id + "F8", { "sketchPlane" : qUnion([Q0])});
            skCircle(sketch, "E34", {"center": v(0, -98.5) * mm, "radius": 11 * mm});
            skCircle(sketch, "E35", {"center": v(0, -98.5) * mm, "radius": 10 * mm});
            skCircle(sketch, "E36", {"center": v(0, -0.8) * mm, "radius": 36.51 * mm});
            skCircle(sketch, "E37", {"center": v(0, -0.8) * mm, "radius": 37.51 * mm});
            skSolve(sketch);
        }
        {
            var Q0;
            {var subQ0=sQuery(id+"F8.wireOp",EDGE,"E36");var subQ1=makeQuery(id+"F5.opExtrude","CAP_EDGE",EDGE,{"disambiguationData":[OSD([sQuery(id+"F0.wireOp",EDGE,"E28")])],"isStart":false});var subQ2=makeQuery(id+"F8.imprint","INTERSECT",VERTEX,{"disambiguationData":[OD(1.0)],"derivedFrom":[subQ1,subQ0]});Q0=makeQuery(id+"F8.imprint","IMPRINT",FACE,{"disambiguationData":[TD([[makeQuery(id+"F8.imprint","IMPRINT",EDGE,{"disambiguationData":[TD([[subQ2,-1.0]])],"derivedFrom":subQ0}),-1.0]])]});}
            var Q1;
            {var subQ0=sQuery(id+"F8.wireOp",EDGE,"E36");var subQ1=makeQuery(id+"F5.opExtrude","CAP_EDGE",EDGE,{"disambiguationData":[OSD([sQuery(id+"F0.wireOp",EDGE,"E17.right")])],"isStart":false});var subQ2=makeQuery(id+"F8.imprint","INTERSECT",VERTEX,{"derivedFrom":[subQ1,subQ0]});Q1=makeQuery(id+"F8.imprint","IMPRINT",FACE,{"disambiguationData":[TD([[makeQuery(id+"F8.imprint","IMPRINT",EDGE,{"disambiguationData":[TD([[subQ2,-1.0]])],"derivedFrom":subQ0}),-1.0]])]});}
            var Q2;
            {var subQ0=sQuery(id+"F8.wireOp",EDGE,"E34");var subQ1=makeQuery(id+"F5.opExtrude","CAP_EDGE",EDGE,{"disambiguationData":[OSD([sQuery(id+"F0.wireOp",EDGE,"E17.left")])],"isStart":false});var subQ2=makeQuery(id+"F8.imprint","INTERSECT",VERTEX,{"derivedFrom":[subQ1,subQ0]});Q2=makeQuery(id+"F8.imprint","IMPRINT",FACE,{"disambiguationData":[TD([[makeQuery(id+"F8.imprint","IMPRINT",EDGE,{"disambiguationData":[TD([[subQ2,-1.0]])],"derivedFrom":subQ0}),1.0]])]});}
            var Q3;
            {var subQ0=sQuery(id+"F8.wireOp",EDGE,"E34");var subQ1=makeQuery(id+"F5.opExtrude","CAP_EDGE",EDGE,{"disambiguationData":[OSD([sQuery(id+"F0.wireOp",EDGE,"E17.right")])],"isStart":false});var subQ2=makeQuery(id+"F8.imprint","INTERSECT",VERTEX,{"derivedFrom":[subQ1,subQ0]});Q3=makeQuery(id+"F8.imprint","IMPRINT",FACE,{"disambiguationData":[TD([[makeQuery(id+"F8.imprint","IMPRINT",EDGE,{"disambiguationData":[TD([[subQ2,1.0]])],"derivedFrom":subQ0}),1.0]])]});}
            var Q4;
            {var subQ0=sQuery(id+"F8.wireOp",EDGE,"E36");var subQ1=makeQuery(id+"F5.opExtrude","CAP_EDGE",EDGE,{"disambiguationData":[OSD([sQuery(id+"F0.wireOp",EDGE,"E22")])],"isStart":false});var subQ2=makeQuery(id+"F8.imprint","INTERSECT",VERTEX,{"derivedFrom":[subQ1,subQ0]});Q4=makeQuery(id+"F8.imprint","IMPRINT",FACE,{"disambiguationData":[TD([[makeQuery(id+"F8.imprint","IMPRINT",EDGE,{"disambiguationData":[TD([[subQ2,-1.0]])],"derivedFrom":subQ0}),-1.0]])]});}
            extrude(context, id + "F9", {"entities" : qUnion([Q0, Q1, Q2, Q3, Q4]), "operationType" : NewBodyOperationType.REMOVE, "oppositeDirection" : true, "depth" : .3 * mm});
        }
        {
            var Q0;
            {var subQ0=sQuery(id+"F0.wireOp",EDGE,"E17.left");var subQ1=sQuery(id+"F0.wireOp",EDGE,"E9");var subQ2=sQuery(id+"F0.wireOp",EDGE,"E17.right");var subQ3=sQuery(id+"F0.wireOp",EDGE,"E2");var subQ5=sQuery(id+"F0.wireOp",EDGE,"E28");Q0=makeQuery(id+"F9.boolean.opBoolean","SPLIT",FACE,{"disambiguationData":[TD([makeQuery(id+"F5.opExtrude","SWEPT_FACE",FACE,{"disambiguationData":[OSD([subQ3])]})])],"derivedFrom":makeQuery(id+"F5.opExtrude","CAP_FACE",FACE,{"disambiguationData":[OSD([subQ3,subQ1,subQ0,subQ2,sQuery(id+"F0.wireOp",EDGE,"E19"),sQuery(id+"F0.wireOp",EDGE,"E22"),sQuery(id+"F0.wireOp",EDGE,"E23"),subQ5])],"isStart":false})});}
            var sketch = newSketch(context, id + "F10", { "sketchPlane" : qUnion([Q0])});
            skCircle(sketch, "E38", {"center": v(0, 0) * mm, "radius": 10.46 * mm});
            skCircle(sketch, "E39", {"center": v(0, 0) * mm, "radius": 11.99 * mm});
            skCircle(sketch, "E40", {"center": v(0, 0) * mm, "radius": 17.56 * mm});
            skCircle(sketch, "E41", {"center": v(0, 0) * mm, "radius": 19.24 * mm});
            skCircle(sketch, "E42", {"center": v(0, 0) * mm, "radius": 27.43 * mm});
            skCircle(sketch, "E43", {"center": v(0, 0) * mm, "radius": 29.16 * mm});
            skCircle(sketch, "E44", {"center": v(0, 0) * mm, "radius": 2.19 * mm});
            skSolve(sketch);
        }
        {
            var Q0;
            {var subQ0=sQuery(id+"F10.wireOp",EDGE,"E42");var subQ1=sQuery(id+"F0.wireOp",EDGE,"E9");var subQ2=makeQuery(id+"F5.opExtrude","CAP_EDGE",EDGE,{"disambiguationData":[OSD([subQ1]),TDD([makeQuery(id+"F0.imprint","IMPRINT",EDGE,{"derivedFrom":subQ1})])],"isStart":false});var subQ3=makeQuery(id+"F10.imprint","INTERSECT",VERTEX,{"disambiguationData":[OD(0.0)],"derivedFrom":[subQ2,subQ0]});Q0=makeQuery(id+"F10.imprint","IMPRINT",FACE,{"disambiguationData":[TD([[makeQuery(id+"F10.imprint","IMPRINT",EDGE,{"disambiguationData":[TD([[subQ3,1.0]])],"derivedFrom":subQ0}),-1.0]])]});}
            var Q1;
            Q1=makeQuery(id+"F10.imprint","IMPRINT",FACE,{"disambiguationData":[TD([[makeQuery(id+"F10.imprint","IMPRINT",EDGE,{"derivedFrom":sQuery(id+"F10.wireOp",EDGE,"E40")}),-1.0]])]});
            var Q2;
            Q2=makeQuery(id+"F10.imprint","IMPRINT",FACE,{"disambiguationData":[TD([[makeQuery(id+"F10.imprint","IMPRINT",EDGE,{"derivedFrom":sQuery(id+"F10.wireOp",EDGE,"E38")}),-1.0]])]});
            var Q3;
            Q3=makeQuery(id+"F10.imprint","IMPRINT",FACE,{"disambiguationData":[TD([[makeQuery(id+"F10.imprint","IMPRINT",EDGE,{"derivedFrom":sQuery(id+"F10.wireOp",EDGE,"E44")}),1.0]])]});
            var Q4;
            Q4=makeQuery(id+"F10.imprint","IMPRINT",FACE,{"disambiguationData":[TD([[makeQuery(id+"F10.imprint","IMPRINT",EDGE,{"derivedFrom":sQuery(id+"F10.wireOp",EDGE,"E42")}),-1.0]])]});
            extrude(context, id + "F11", {"entities" : qUnion([Q0, Q1, Q2, Q3, Q4]), "operationType" : NewBodyOperationType.REMOVE, "oppositeDirection" : true, "depth" : 0.3 * mm});
        }
    });
